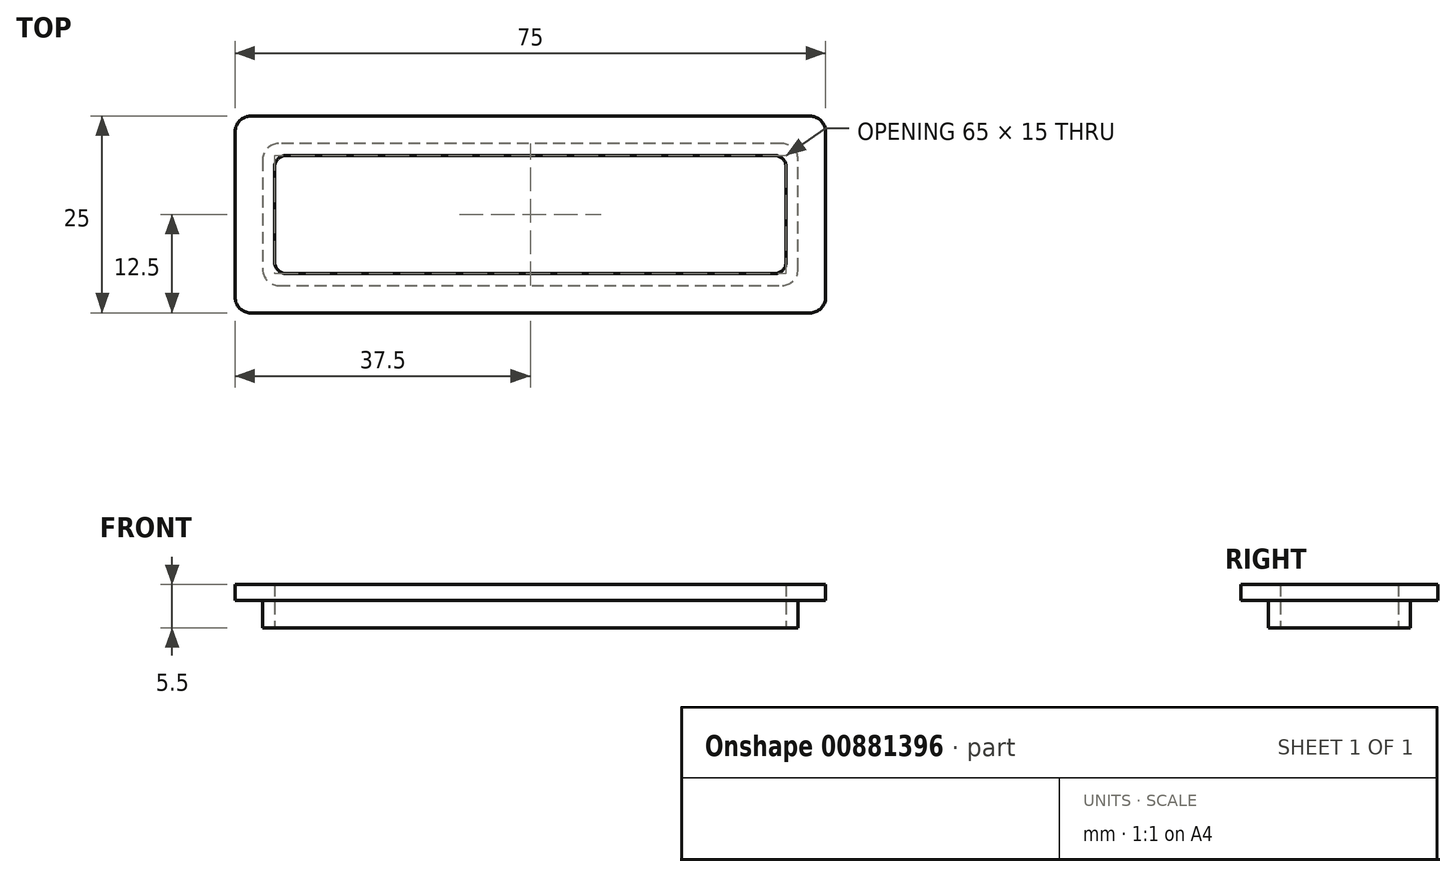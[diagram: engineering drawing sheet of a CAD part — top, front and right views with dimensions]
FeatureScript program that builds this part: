
annotation { "Feature Type Name" : "Feature", "Feature Type Description" : "" }
export const myFeature = defineFeature(function(context is Context, id is Id, definition is map)
    precondition{}
    {
        {
            var Q0;
            Q0=qCreatedBy(makeId("Top.planeOp"),FACE);
            var sketch = newSketch(context, id + "F0", { "sketchPlane" : qUnion([Q0])});
            skLineSegment(sketch, "E0.bottom", {"start": v(32.5, -7.5) * mm, "end": v(-32.5, -7.5) * mm});
            skLineSegment(sketch, "E0.top", {"start": v(32.5, 7.5) * mm, "end": v(-32.5, 7.5) * mm});
            skLineSegment(sketch, "E0.left", {"start": v(32.5, -7.5) * mm, "end": v(32.5, 7.5) * mm});
            skLineSegment(sketch, "E0.right", {"start": v(-32.5, -7.5) * mm, "end": v(-32.5, 7.5) * mm});
            skPoint(sketch, "E0.middle", {"position": v(0, 0) * mm});
            skLineSegment(sketch, "E1.0", {"start": v(37.5, 12.5) * mm, "end": v(-37.5, 12.5) * mm});
            skLineSegment(sketch, "E1.1", {"start": v(37.5, -12.5) * mm, "end": v(37.5, 12.5) * mm});
            skLineSegment(sketch, "E1.2", {"start": v(37.5, -12.5) * mm, "end": v(-37.5, -12.5) * mm});
            skLineSegment(sketch, "E1.3", {"start": v(-37.5, -12.5) * mm, "end": v(-37.5, 12.5) * mm});
            skSolve(sketch);
        }
        {
            var Q0;
            Q0=makeQuery(id+"F0.imprint","IMPRINT",FACE,{"disambiguationData":[TD([[makeQuery(id+"F0.imprint","IMPRINT",EDGE,{"derivedFrom":sQuery(id+"F0.wireOp",EDGE,"E0.bottom")}),1.0]])]});
            extrude(context, id + "F1", {"entities" : qUnion([Q0]), "depth" : 2 * mm});
        }
        {
            var Q0;
            Q0=makeQuery(id+"F1.opExtrude","SWEPT_EDGE",EDGE,{"disambiguationData":[OSD([sQuery(id+"F0.wireOp",EDGE,"E1.0"),sQuery(id+"F0.wireOp",EDGE,"E1.1")])]});
            var Q1;
            Q1=makeQuery(id+"F1.opExtrude","SWEPT_EDGE",EDGE,{"disambiguationData":[OSD([sQuery(id+"F0.wireOp",EDGE,"E1.1"),sQuery(id+"F0.wireOp",EDGE,"E1.2")])]});
            var Q2;
            Q2=makeQuery(id+"F1.opExtrude","SWEPT_EDGE",EDGE,{"disambiguationData":[OSD([sQuery(id+"F0.wireOp",EDGE,"E1.2"),sQuery(id+"F0.wireOp",EDGE,"E1.3")])]});
            var Q3;
            Q3=makeQuery(id+"F1.opExtrude","SWEPT_EDGE",EDGE,{"disambiguationData":[OSD([sQuery(id+"F0.wireOp",EDGE,"E1.0"),sQuery(id+"F0.wireOp",EDGE,"E1.3")])]});
            fillet(context, id + "F2", {"entities" : qUnion([Q0, Q1, Q2, Q3]), "radius" : 2 * mm, "tangentPropagation" : true, "allowEdgeOverflow" : false});
        }
        {
            var Q0;
            Q0=makeQuery(id+"F1.opExtrude","CAP_FACE",FACE,{"disambiguationData":[OSD([sQuery(id+"F0.wireOp",EDGE,"E0.bottom"),sQuery(id+"F0.wireOp",EDGE,"E0.top"),sQuery(id+"F0.wireOp",EDGE,"E0.left"),sQuery(id+"F0.wireOp",EDGE,"E0.right"),sQuery(id+"F0.wireOp",EDGE,"E1.0"),sQuery(id+"F0.wireOp",EDGE,"E1.1"),sQuery(id+"F0.wireOp",EDGE,"E1.2"),sQuery(id+"F0.wireOp",EDGE,"E1.3")])],"isStart":true});
            var sketch = newSketch(context, id + "F3", { "sketchPlane" : qUnion([Q0])});
            skPoint(sketch, "E2", {"position": v(32.5, -7.5) * mm});
            skPoint(sketch, "E3", {"position": v(32.5, 7.5) * mm});
            skPoint(sketch, "E4", {"position": v(-32.5, 7.5) * mm});
            skPoint(sketch, "E5", {"position": v(-32.5, -7.5) * mm});
            skLineSegment(sketch, "E6", {"start": v(32.5, -7.5) * mm, "end": v(-32.5, -7.5) * mm});
            skLineSegment(sketch, "E7", {"start": v(-32.5, -7.5) * mm, "end": v(-32.5, 7.5) * mm});
            skLineSegment(sketch, "E8", {"start": v(-32.5, 7.5) * mm, "end": v(32.5, 7.5) * mm});
            skLineSegment(sketch, "E9", {"start": v(32.5, 7.5) * mm, "end": v(32.5, -7.5) * mm});
            skLineSegment(sketch, "E10.0", {"start": v(34, -9) * mm, "end": v(-34, -9) * mm});
            skLineSegment(sketch, "E10.1", {"start": v(34, 9) * mm, "end": v(34, -9) * mm});
            skLineSegment(sketch, "E10.2", {"start": v(-34, 9) * mm, "end": v(34, 9) * mm});
            skLineSegment(sketch, "E10.3", {"start": v(-34, -9) * mm, "end": v(-34, 9) * mm});
            skSolve(sketch);
        }
        {
            var Q0;
            Q0=makeQuery(id+"F3.imprint","IMPRINT",FACE,{"disambiguationData":[TD([[makeQuery(id+"F3.imprint","IMPRINT",EDGE,{"derivedFrom":sQuery(id+"F3.wireOp",EDGE,"E6")}),1.0]])]});
            extrude(context, id + "F4", {"entities" : qUnion([Q0]), "operationType" : NewBodyOperationType.ADD, "depth" : 3.5 * mm});
        }
        {
            var Q0;
            Q0=makeQuery(id+"F4.opExtrude","SWEPT_EDGE",EDGE,{"disambiguationData":[OSD([sQuery(id+"F3.wireOp",EDGE,"E10.1"),sQuery(id+"F3.wireOp",EDGE,"E10.2")])]});
            var Q1;
            Q1=makeQuery(id+"F4.opExtrude","SWEPT_EDGE",EDGE,{"disambiguationData":[OSD([sQuery(id+"F3.wireOp",EDGE,"E10.2"),sQuery(id+"F3.wireOp",EDGE,"E10.3")])]});
            var Q2;
            Q2=makeQuery(id+"F4.opExtrude","SWEPT_EDGE",EDGE,{"disambiguationData":[OSD([sQuery(id+"F3.wireOp",EDGE,"E10.0"),sQuery(id+"F3.wireOp",EDGE,"E10.3")])]});
            var Q3;
            Q3=makeQuery(id+"F4.opExtrude","SWEPT_EDGE",EDGE,{"disambiguationData":[OSD([sQuery(id+"F3.wireOp",EDGE,"E10.0"),sQuery(id+"F3.wireOp",EDGE,"E10.1")])]});
            fillet(context, id + "F5", {"entities" : qUnion([Q0, Q1, Q2, Q3]), "radius" : 2 * mm, "tangentPropagation" : true, "allowEdgeOverflow" : false});
        }
        {
            var Q0;
            Q0=makeQuery(id+"F4.boolean.opBoolean","MERGE",EDGE,{"derivedFrom":[makeQuery(id+"F1.opExtrude","SWEPT_EDGE",EDGE,{"disambiguationData":[OSD([sQuery(id+"F0.wireOp",EDGE,"E0.top"),sQuery(id+"F0.wireOp",EDGE,"E0.left")])]}),makeQuery(id+"F4.opExtrude","SWEPT_EDGE",EDGE,{"disambiguationData":[OSD([sQuery(id+"F3.wireOp",EDGE,"E6"),sQuery(id+"F3.wireOp",EDGE,"E9")])]})]});
            var Q1;
            Q1=makeQuery(id+"F4.boolean.opBoolean","MERGE",EDGE,{"derivedFrom":[makeQuery(id+"F1.opExtrude","SWEPT_EDGE",EDGE,{"disambiguationData":[OSD([sQuery(id+"F0.wireOp",EDGE,"E0.bottom"),sQuery(id+"F0.wireOp",EDGE,"E0.left")])]}),makeQuery(id+"F4.opExtrude","SWEPT_EDGE",EDGE,{"disambiguationData":[OSD([sQuery(id+"F3.wireOp",EDGE,"E8"),sQuery(id+"F3.wireOp",EDGE,"E9")])]})]});
            var Q2;
            Q2=makeQuery(id+"F4.boolean.opBoolean","MERGE",EDGE,{"derivedFrom":[makeQuery(id+"F1.opExtrude","SWEPT_EDGE",EDGE,{"disambiguationData":[OSD([sQuery(id+"F0.wireOp",EDGE,"E0.bottom"),sQuery(id+"F0.wireOp",EDGE,"E0.right")])]}),makeQuery(id+"F4.opExtrude","SWEPT_EDGE",EDGE,{"disambiguationData":[OSD([sQuery(id+"F3.wireOp",EDGE,"E7"),sQuery(id+"F3.wireOp",EDGE,"E8")])]})]});
            var Q3;
            Q3=makeQuery(id+"F4.boolean.opBoolean","MERGE",EDGE,{"derivedFrom":[makeQuery(id+"F1.opExtrude","SWEPT_EDGE",EDGE,{"disambiguationData":[OSD([sQuery(id+"F0.wireOp",EDGE,"E0.top"),sQuery(id+"F0.wireOp",EDGE,"E0.right")])]}),makeQuery(id+"F4.opExtrude","SWEPT_EDGE",EDGE,{"disambiguationData":[OSD([sQuery(id+"F3.wireOp",EDGE,"E6"),sQuery(id+"F3.wireOp",EDGE,"E7")])]})]});
            fillet(context, id + "F6", {"entities" : qUnion([Q0, Q1, Q2, Q3]), "radius" : 1.5 * mm, "tangentPropagation" : true, "allowEdgeOverflow" : false});
        }
    });
